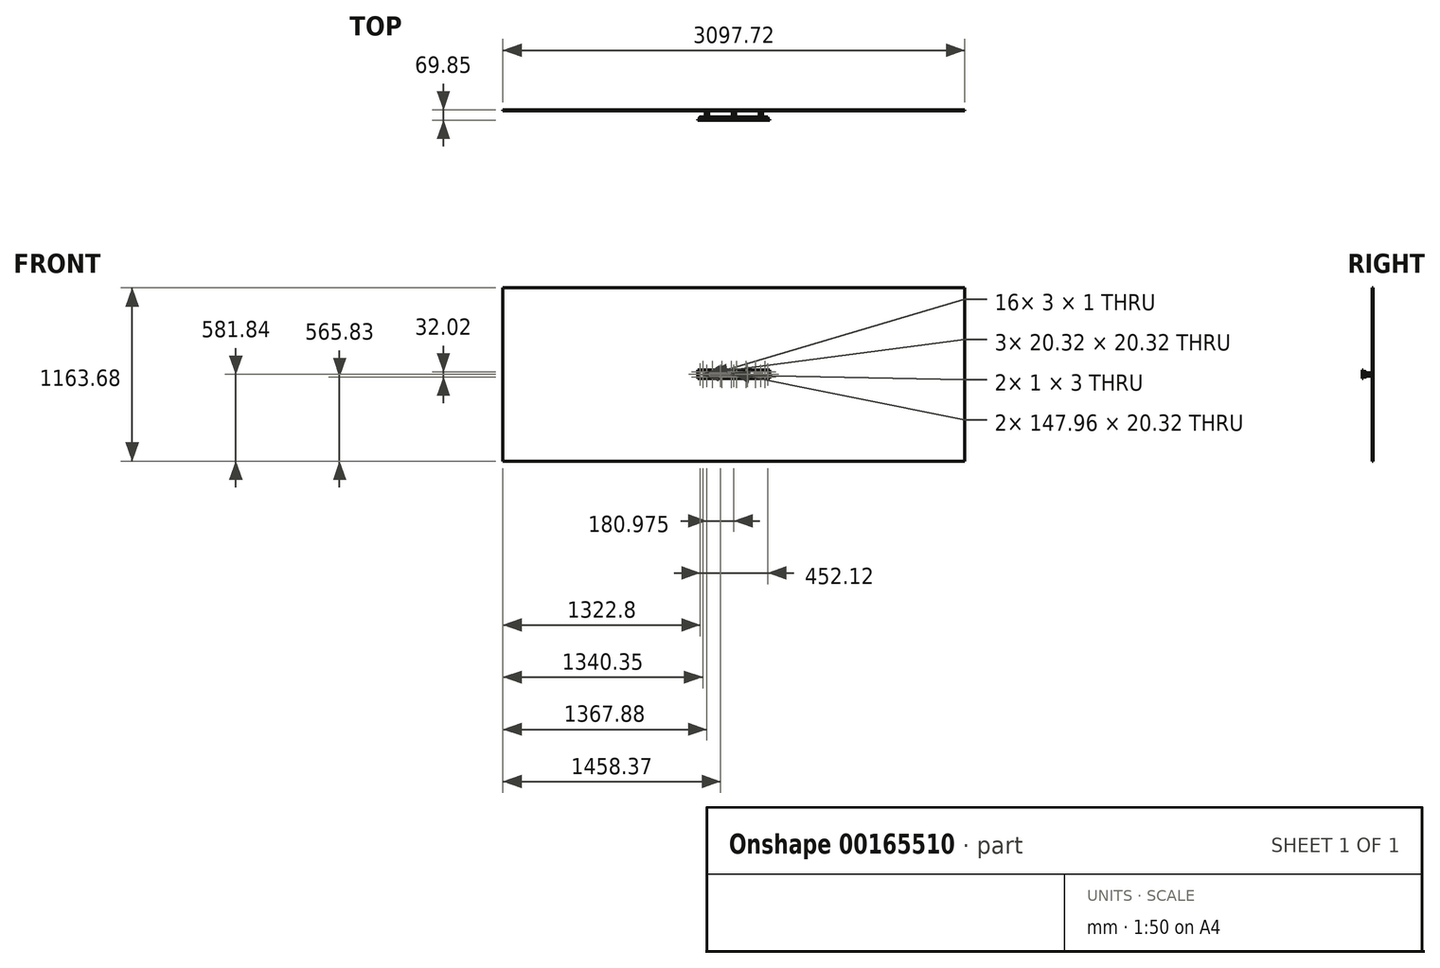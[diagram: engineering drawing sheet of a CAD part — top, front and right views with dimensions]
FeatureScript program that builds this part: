
annotation { "Feature Type Name" : "Feature", "Feature Type Description" : "" }
export const myFeature = defineFeature(function(context is Context, id is Id, definition is map)
    precondition{}
    {
        {
            var Q0;
            Q0=qCreatedBy(makeId("Front.planeOp"),FACE);
            var sketch = newSketch(context, id + "F0", { "sketchPlane" : qUnion([Q0])});
            skLineSegment(sketch, "E0.bottom", {"start": v(10.16, -10.16) * mm, "end": v(-10.16, -10.16) * mm});
            skLineSegment(sketch, "E0.top", {"start": v(10.16, 10.16) * mm, "end": v(-10.16, 10.16) * mm});
            skLineSegment(sketch, "E0.left", {"start": v(10.16, -10.16) * mm, "end": v(10.16, 10.16) * mm});
            skLineSegment(sketch, "E0.right", {"start": v(-10.16, -10.16) * mm, "end": v(-10.16, 10.16) * mm});
            skPoint(sketch, "E0.middle", {"position": v(0, 0) * mm});
            skLineSegment(sketch, "E1.1.0.0", {"start": v(191.14, 10.16) * mm, "end": v(170.82, 10.16) * mm});
            skLineSegment(sketch, "E1.1.0.1", {"start": v(170.82, -10.16) * mm, "end": v(170.82, 10.16) * mm});
            skLineSegment(sketch, "E1.1.0.2", {"start": v(191.14, -10.16) * mm, "end": v(170.82, -10.16) * mm});
            skLineSegment(sketch, "E1.1.0.3", {"start": v(191.14, -10.16) * mm, "end": v(191.14, 10.16) * mm});
            skLineSegment(sketch, "E1.direction1", {"start": v(-10.16, 10.16) * mm, "end": v(170.82, 10.16) * mm, "construction": true});
            skLineSegment(sketch, "E2.MirrorCS", {"start": v(-170.82, -10.16) * mm, "end": v(-170.82, 10.16) * mm});
            skLineSegment(sketch, "E3.MirrorCS", {"start": v(-191.14, 10.16) * mm, "end": v(-170.82, 10.16) * mm});
            skLineSegment(sketch, "E4.MirrorCS", {"start": v(-191.14, -10.16) * mm, "end": v(-170.82, -10.16) * mm});
            skLineSegment(sketch, "E5.MirrorCS", {"start": v(-191.14, -10.16) * mm, "end": v(-191.14, 10.16) * mm});
            skSolve(sketch);
        }
        {
            var Q0;
            Q0=qSketchRegion(id+"F0",true);
            extrude(context, id + "F1", {"entities" : qUnion([Q0]), "depth" : 63.5 * mm});
        }
        {
            var Q0;
            Q0=makeQuery(id+"F1.opExtrude","CAP_FACE",FACE,{"disambiguationData":[OSD([sQuery(id+"F0.wireOp",EDGE,"E2.MirrorCS"),sQuery(id+"F0.wireOp",EDGE,"E3.MirrorCS"),sQuery(id+"F0.wireOp",EDGE,"E4.MirrorCS"),sQuery(id+"F0.wireOp",EDGE,"E5.MirrorCS")])],"isStart":false});
            var sketch = newSketch(context, id + "F2", { "sketchPlane" : qUnion([Q0])});
            skLineSegment(sketch, "E6.bottom", {"start": v(241.3, -28.57) * mm, "end": v(-241.3, -28.58) * mm});
            skLineSegment(sketch, "E6.top", {"start": v(241.3, 28.58) * mm, "end": v(-241.3, 28.57) * mm});
            skLineSegment(sketch, "E6.left", {"start": v(241.3, -28.57) * mm, "end": v(241.3, 28.58) * mm});
            skLineSegment(sketch, "E6.right", {"start": v(-241.3, -28.58) * mm, "end": v(-241.3, 28.57) * mm});
            skPoint(sketch, "E6.middle", {"position": v(0, 0) * mm});
            skSolve(sketch);
        }
        {
            var Q0;
            Q0=qSketchRegion(id+"F2",true);
            extrude(context, id + "F3", {"entities" : qUnion([Q0]), "depth" : 6.35 * mm});
        }
        {
            var Q0;
            Q0=makeQuery(id+"F3.opExtrude","CAP_FACE",FACE,{"disambiguationData":[OSD([sQuery(id+"F2.wireOp",EDGE,"E6.bottom"),sQuery(id+"F2.wireOp",EDGE,"E6.top"),sQuery(id+"F2.wireOp",EDGE,"E6.left"),sQuery(id+"F2.wireOp",EDGE,"E6.right")])],"isStart":true});
            cPlane(context, id + "F4", {"entities" : qUnion([Q0]), "cplaneType" : CPlaneType.OFFSET, "offset" : 3 * mm, "width" : 152.4 * mm, "height" : 152.4 * mm});
        }
        {
            var Q0;
            Q0=qCreatedBy(id+"F4.planeOp",FACE);
            var sketch = newSketch(context, id + "F5", { "sketchPlane" : qUnion([Q0])});
            skLineSegment(sketch, "E7.bottom", {"start": v(228.6, -19.05) * mm, "end": v(-228.6, -19.05) * mm});
            skLineSegment(sketch, "E7.top", {"start": v(228.6, 19.05) * mm, "end": v(-228.6, 19.05) * mm});
            skLineSegment(sketch, "E7.left", {"start": v(228.6, -19.05) * mm, "end": v(228.6, 19.05) * mm});
            skLineSegment(sketch, "E7.right", {"start": v(-228.6, -19.05) * mm, "end": v(-228.6, 19.05) * mm});
            skPoint(sketch, "E7.middle", {"position": v(0, 0) * mm});
            skLineSegment(sketch, "E8.1", {"start": v(-191.14, 10.16) * mm, "end": v(-170.82, 10.16) * mm});
            skLineSegment(sketch, "E8.2", {"start": v(-191.14, -10.16) * mm, "end": v(-191.14, 10.16) * mm});
            skLineSegment(sketch, "E8.3", {"start": v(-191.14, -10.16) * mm, "end": v(-170.82, -10.16) * mm});
            skLineSegment(sketch, "E8.4", {"start": v(-170.82, -10.16) * mm, "end": v(-170.82, 10.16) * mm});
            skLineSegment(sketch, "E8.5", {"start": v(-10.16, -10.16) * mm, "end": v(-10.16, 10.16) * mm});
            skLineSegment(sketch, "E8.6", {"start": v(-10.16, 10.16) * mm, "end": v(10.16, 10.16) * mm});
            skLineSegment(sketch, "E8.7", {"start": v(10.16, -10.16) * mm, "end": v(10.16, 10.16) * mm});
            skLineSegment(sketch, "E8.8", {"start": v(-10.16, -10.16) * mm, "end": v(10.16, -10.16) * mm});
            skLineSegment(sketch, "E8.9", {"start": v(191.14, 10.16) * mm, "end": v(170.82, 10.16) * mm});
            skLineSegment(sketch, "E8.10", {"start": v(170.82, -10.16) * mm, "end": v(170.82, 10.16) * mm});
            skLineSegment(sketch, "E8.11", {"start": v(191.14, -10.16) * mm, "end": v(170.82, -10.16) * mm});
            skLineSegment(sketch, "E8.12", {"start": v(191.14, -10.16) * mm, "end": v(191.14, 10.16) * mm});
            skLineSegment(sketch, "E9", {"start": v(0, 19.05) * mm, "end": v(0, 10.16) * mm, "construction": true});
            skLineSegment(sketch, "E10.0", {"start": v(-241.3, -28.57) * mm, "end": v(241.3, -28.58) * mm, "construction": true});
            skLineSegment(sketch, "E10.1", {"start": v(241.3, -28.58) * mm, "end": v(241.3, 28.57) * mm, "construction": true});
            skLineSegment(sketch, "E10.2", {"start": v(-241.3, 28.58) * mm, "end": v(241.3, 28.57) * mm, "construction": true});
            skLineSegment(sketch, "E10.3", {"start": v(-241.3, -28.57) * mm, "end": v(-241.3, 28.58) * mm, "construction": true});
            skLineSegment(sketch, "E11", {"start": v(-226.06, -19.05) * mm, "end": v(-226.06, 19.05) * mm, "construction": true});
            skLineSegment(sketch, "E12.bottom", {"start": v(-226.56, 1.5) * mm, "end": v(-225.56, 1.5) * mm});
            skLineSegment(sketch, "E12.top", {"start": v(-226.56, -1.5) * mm, "end": v(-225.56, -1.5) * mm});
            skLineSegment(sketch, "E12.left", {"start": v(-226.56, 1.5) * mm, "end": v(-226.56, -1.5) * mm});
            skLineSegment(sketch, "E12.right", {"start": v(-225.56, 1.5) * mm, "end": v(-225.56, -1.5) * mm});
            skPoint(sketch, "E12.middle", {"position": v(-226.06, 0) * mm});
            skLineSegment(sketch, "E13.MirrorCS", {"start": v(226.56, -1.5) * mm, "end": v(225.56, -1.5) * mm});
            skLineSegment(sketch, "E14.MirrorCS", {"start": v(225.56, 1.5) * mm, "end": v(225.56, -1.5) * mm});
            skPoint(sketch, "E15.MirrorP", {"position": v(226.06, 0) * mm});
            skLineSegment(sketch, "E16.MirrorCS", {"start": v(226.56, 1.5) * mm, "end": v(226.56, -1.5) * mm});
            skLineSegment(sketch, "E17.MirrorCS", {"start": v(226.56, 1.5) * mm, "end": v(225.56, 1.5) * mm});
            skLineSegment(sketch, "E18.bottom", {"start": v(16.51, 10.16) * mm, "end": v(164.47, 10.16) * mm});
            skLineSegment(sketch, "E18.top", {"start": v(16.51, -10.16) * mm, "end": v(164.47, -10.16) * mm});
            skLineSegment(sketch, "E18.left", {"start": v(16.51, 10.16) * mm, "end": v(16.51, -10.16) * mm});
            skLineSegment(sketch, "E18.right", {"start": v(164.47, 10.16) * mm, "end": v(164.47, -10.16) * mm});
            skPoint(sketch, "E18.middle", {"position": v(90.49, 0) * mm});
            skLineSegment(sketch, "E19.MirrorCS", {"start": v(-16.51, -10.16) * mm, "end": v(-164.47, -10.16) * mm});
            skLineSegment(sketch, "E20.MirrorCS", {"start": v(-164.47, 10.16) * mm, "end": v(-164.47, -10.16) * mm});
            skLineSegment(sketch, "E21.MirrorCS", {"start": v(-16.51, 10.16) * mm, "end": v(-164.47, 10.16) * mm});
            skLineSegment(sketch, "E22.MirrorCS", {"start": v(-16.51, 10.16) * mm, "end": v(-16.51, -10.16) * mm});
            skLineSegment(sketch, "E23.bottom", {"start": v(-16.5, 16.51) * mm, "end": v(-19.5, 16.51) * mm});
            skLineSegment(sketch, "E23.top", {"start": v(-16.5, 15.51) * mm, "end": v(-19.5, 15.51) * mm});
            skLineSegment(sketch, "E23.left", {"start": v(-16.51, 16.5) * mm, "end": v(-16.51, 15.5) * mm});
            skLineSegment(sketch, "E23.right", {"start": v(-19.51, 16.51) * mm, "end": v(-19.51, 15.5) * mm});
            skLineSegment(sketch, "E24.1.0.0", {"start": v(-80, 16.51) * mm, "end": v(-83, 16.51) * mm});
            skLineSegment(sketch, "E24.1.0.1", {"start": v(-80, 16.5) * mm, "end": v(-80, 15.5) * mm});
            skLineSegment(sketch, "E24.1.0.2", {"start": v(-80, 15.51) * mm, "end": v(-83, 15.51) * mm});
            skLineSegment(sketch, "E24.1.0.3", {"start": v(-83.01, 16.5) * mm, "end": v(-83.01, 15.5) * mm});
            skLineSegment(sketch, "E24.2.0.0", {"start": v(-143.5, 16.51) * mm, "end": v(-146.5, 16.51) * mm});
            skLineSegment(sketch, "E24.2.0.1", {"start": v(-143.5, 16.5) * mm, "end": v(-143.5, 15.5) * mm});
            skLineSegment(sketch, "E24.2.0.2", {"start": v(-143.5, 15.51) * mm, "end": v(-146.5, 15.51) * mm});
            skLineSegment(sketch, "E24.2.0.3", {"start": v(-146.5, 16.5) * mm, "end": v(-146.5, 15.5) * mm});
            skLineSegment(sketch, "E24.3.0.0", {"start": v(-207, 16.51) * mm, "end": v(-210, 16.51) * mm});
            skLineSegment(sketch, "E24.3.0.1", {"start": v(-207, 16.5) * mm, "end": v(-207, 15.5) * mm});
            skLineSegment(sketch, "E24.3.0.2", {"start": v(-207, 15.51) * mm, "end": v(-210, 15.51) * mm});
            skLineSegment(sketch, "E24.3.0.3", {"start": v(-210, 16.5) * mm, "end": v(-210, 15.5) * mm});
            skLineSegment(sketch, "E24.direction1", {"start": v(-19.5, 16.51) * mm, "end": v(-83, 16.51) * mm, "construction": true});
            skLineSegment(sketch, "E25.MirrorCS", {"start": v(19.51, 16.51) * mm, "end": v(19.51, 15.5) * mm});
            skLineSegment(sketch, "E26.MirrorCS", {"start": v(83.01, 16.5) * mm, "end": v(83.01, 15.5) * mm});
            skLineSegment(sketch, "E27.MirrorCS", {"start": v(207, 15.51) * mm, "end": v(210, 15.51) * mm});
            skLineSegment(sketch, "E28.MirrorCS", {"start": v(80, 15.51) * mm, "end": v(83, 15.51) * mm});
            skLineSegment(sketch, "E29.MirrorCS", {"start": v(143.5, 16.5) * mm, "end": v(143.5, 15.5) * mm});
            skLineSegment(sketch, "E30.MirrorCS", {"start": v(16.5, 15.51) * mm, "end": v(19.5, 15.51) * mm});
            skLineSegment(sketch, "E31.MirrorCS", {"start": v(143.5, 15.51) * mm, "end": v(146.5, 15.51) * mm});
            skLineSegment(sketch, "E32.MirrorCS", {"start": v(207, 16.51) * mm, "end": v(210, 16.51) * mm});
            skLineSegment(sketch, "E33.MirrorCS", {"start": v(143.5, 16.51) * mm, "end": v(146.5, 16.51) * mm});
            skLineSegment(sketch, "E34.MirrorCS", {"start": v(146.5, 16.5) * mm, "end": v(146.5, 15.5) * mm});
            skLineSegment(sketch, "E35.MirrorCS", {"start": v(80, 16.51) * mm, "end": v(83, 16.51) * mm});
            skLineSegment(sketch, "E36.MirrorCS", {"start": v(210, 16.5) * mm, "end": v(210, 15.5) * mm});
            skLineSegment(sketch, "E37.MirrorCS", {"start": v(16.5, 16.51) * mm, "end": v(19.5, 16.51) * mm});
            skLineSegment(sketch, "E38.MirrorCS", {"start": v(80, 16.5) * mm, "end": v(80, 15.5) * mm});
            skLineSegment(sketch, "E39.MirrorCS", {"start": v(16.51, 16.5) * mm, "end": v(16.51, 15.5) * mm});
            skLineSegment(sketch, "E40.MirrorCS", {"start": v(207, 16.5) * mm, "end": v(207, 15.5) * mm});
            skLineSegment(sketch, "E41.MirrorCS", {"start": v(19.5, 16.51) * mm, "end": v(83, 16.51) * mm, "construction": true});
            skLineSegment(sketch, "E42.MirrorCS", {"start": v(19.51, -16.51) * mm, "end": v(19.51, -15.5) * mm});
            skLineSegment(sketch, "E43.MirrorCS", {"start": v(-16.5, -16.5) * mm, "end": v(-19.5, -16.5) * mm});
            skLineSegment(sketch, "E44.MirrorCS", {"start": v(-19.5, -16.51) * mm, "end": v(-19.5, -15.5) * mm});
            skLineSegment(sketch, "E45.MirrorCS", {"start": v(16.5, -15.51) * mm, "end": v(19.5, -15.51) * mm});
            skLineSegment(sketch, "E46.MirrorCS", {"start": v(80, -15.51) * mm, "end": v(83, -15.51) * mm});
            skLineSegment(sketch, "E47.MirrorCS", {"start": v(-80, -16.5) * mm, "end": v(-83, -16.5) * mm});
            skLineSegment(sketch, "E48.MirrorCS", {"start": v(83.01, -16.5) * mm, "end": v(83.01, -15.5) * mm});
            skLineSegment(sketch, "E49.MirrorCS", {"start": v(-16.5, -15.51) * mm, "end": v(-19.5, -15.51) * mm});
            skLineSegment(sketch, "E50.MirrorCS", {"start": v(16.5, -16.5) * mm, "end": v(19.5, -16.5) * mm});
            skLineSegment(sketch, "E51.MirrorCS", {"start": v(80, -16.5) * mm, "end": v(83, -16.5) * mm});
            skLineSegment(sketch, "E52.MirrorCS", {"start": v(-83, -16.5) * mm, "end": v(-83, -15.5) * mm});
            skLineSegment(sketch, "E53.MirrorCS", {"start": v(143.5, -16.5) * mm, "end": v(146.5, -16.5) * mm});
            skLineSegment(sketch, "E54.MirrorCS", {"start": v(207, -16.5) * mm, "end": v(210, -16.5) * mm});
            skLineSegment(sketch, "E55.MirrorCS", {"start": v(16.51, -16.5) * mm, "end": v(16.51, -15.5) * mm});
            skLineSegment(sketch, "E56.MirrorCS", {"start": v(207, -16.5) * mm, "end": v(207, -15.5) * mm});
            skLineSegment(sketch, "E57.MirrorCS", {"start": v(143.5, -15.51) * mm, "end": v(146.5, -15.51) * mm});
            skLineSegment(sketch, "E58.MirrorCS", {"start": v(-80, -15.51) * mm, "end": v(-83, -15.51) * mm});
            skLineSegment(sketch, "E59.MirrorCS", {"start": v(-16.5, -16.5) * mm, "end": v(-16.5, -15.5) * mm});
            skLineSegment(sketch, "E60.MirrorCS", {"start": v(-80, -16.5) * mm, "end": v(-80, -15.5) * mm});
            skLineSegment(sketch, "E61.MirrorCS", {"start": v(143.5, -16.5) * mm, "end": v(143.5, -15.5) * mm});
            skLineSegment(sketch, "E62.MirrorCS", {"start": v(207, -15.51) * mm, "end": v(210, -15.51) * mm});
            skLineSegment(sketch, "E63.MirrorCS", {"start": v(80, -16.5) * mm, "end": v(80, -15.5) * mm});
            skLineSegment(sketch, "E64.MirrorCS", {"start": v(210, -16.5) * mm, "end": v(210, -15.5) * mm});
            skLineSegment(sketch, "E65.MirrorCS", {"start": v(146.5, -16.5) * mm, "end": v(146.5, -15.5) * mm});
            skLineSegment(sketch, "E66.MirrorCS", {"start": v(19.5, -16.5) * mm, "end": v(83, -16.5) * mm, "construction": true});
            skLineSegment(sketch, "E67.MirrorCS", {"start": v(-19.5, -16.51) * mm, "end": v(-83, -16.51) * mm, "construction": true});
            skLineSegment(sketch, "E68.MirrorCS", {"start": v(-143.5, -16.5) * mm, "end": v(-143.5, -15.5) * mm});
            skLineSegment(sketch, "E69.MirrorCS", {"start": v(-207, -16.5) * mm, "end": v(-207, -15.5) * mm});
            skLineSegment(sketch, "E70.MirrorCS", {"start": v(-210, -16.5) * mm, "end": v(-210, -15.5) * mm});
            skLineSegment(sketch, "E71.MirrorCS", {"start": v(-146.5, -16.5) * mm, "end": v(-146.5, -15.5) * mm});
            skLineSegment(sketch, "E72.MirrorCS", {"start": v(-143.5, -15.51) * mm, "end": v(-146.5, -15.51) * mm});
            skLineSegment(sketch, "E73.MirrorCS", {"start": v(-143.5, -16.5) * mm, "end": v(-146.5, -16.5) * mm});
            skLineSegment(sketch, "E74.MirrorCS", {"start": v(-207, -15.51) * mm, "end": v(-210, -15.51) * mm});
            skLineSegment(sketch, "E75.MirrorCS", {"start": v(-207, -16.5) * mm, "end": v(-210, -16.5) * mm});
            skSolve(sketch);
        }
        {
            var Q0;
            Q0=qSketchRegion(id+"F5",true);
            extrude(context, id + "F6", {"entities" : qUnion([Q0]), "depth" : 12.7 * mm});
        }
        {
            var Q0;
            Q0=makeQuery(id+"F6.opExtrude","SWEPT_EDGE",EDGE,{"disambiguationData":[OSD([sQuery(id+"F5.wireOp",EDGE,"E7.top"),sQuery(id+"F5.wireOp",EDGE,"E7.right")])]});
            var Q1;
            Q1=makeQuery(id+"F6.opExtrude","SWEPT_EDGE",EDGE,{"disambiguationData":[OSD([sQuery(id+"F5.wireOp",EDGE,"E7.bottom"),sQuery(id+"F5.wireOp",EDGE,"E7.right")])]});
            var Q2;
            Q2=makeQuery(id+"F6.opExtrude","SWEPT_EDGE",EDGE,{"disambiguationData":[OSD([sQuery(id+"F5.wireOp",EDGE,"E7.top"),sQuery(id+"F5.wireOp",EDGE,"E7.left")])]});
            var Q3;
            Q3=makeQuery(id+"F6.opExtrude","SWEPT_EDGE",EDGE,{"disambiguationData":[OSD([sQuery(id+"F5.wireOp",EDGE,"E7.bottom"),sQuery(id+"F5.wireOp",EDGE,"E7.left")])]});
            fillet(context, id + "F7", {"entities" : qUnion([Q0, Q1, Q2, Q3]), "radius" : 12.7 * mm, "tangentPropagation" : true, "allowEdgeOverflow" : false});
        }
        {
            var Q0;
            Q0=qCreatedBy(makeId("Front.planeOp"),FACE);
            var sketch = newSketch(context, id + "F8", { "sketchPlane" : qUnion([Q0])});
            skLineSegment(sketch, "E76.bottom", {"start": v(-1548.86, -581.84) * mm, "end": v(1548.86, -581.84) * mm});
            skLineSegment(sketch, "E76.top", {"start": v(-1548.86, 581.84) * mm, "end": v(1548.86, 581.84) * mm});
            skLineSegment(sketch, "E76.left", {"start": v(-1548.86, -581.84) * mm, "end": v(-1548.86, 581.84) * mm});
            skLineSegment(sketch, "E76.right", {"start": v(1548.86, -581.84) * mm, "end": v(1548.86, 581.84) * mm});
            skPoint(sketch, "E76.middle", {"position": v(0, 0) * mm});
            skSolve(sketch);
        }
        {
            var Q0;
            Q0=qSketchRegion(id+"F8",true);
            extrude(context, id + "F9", {"entities" : qUnion([Q0]), "depth" : 6.35 * mm});
        }
    });
